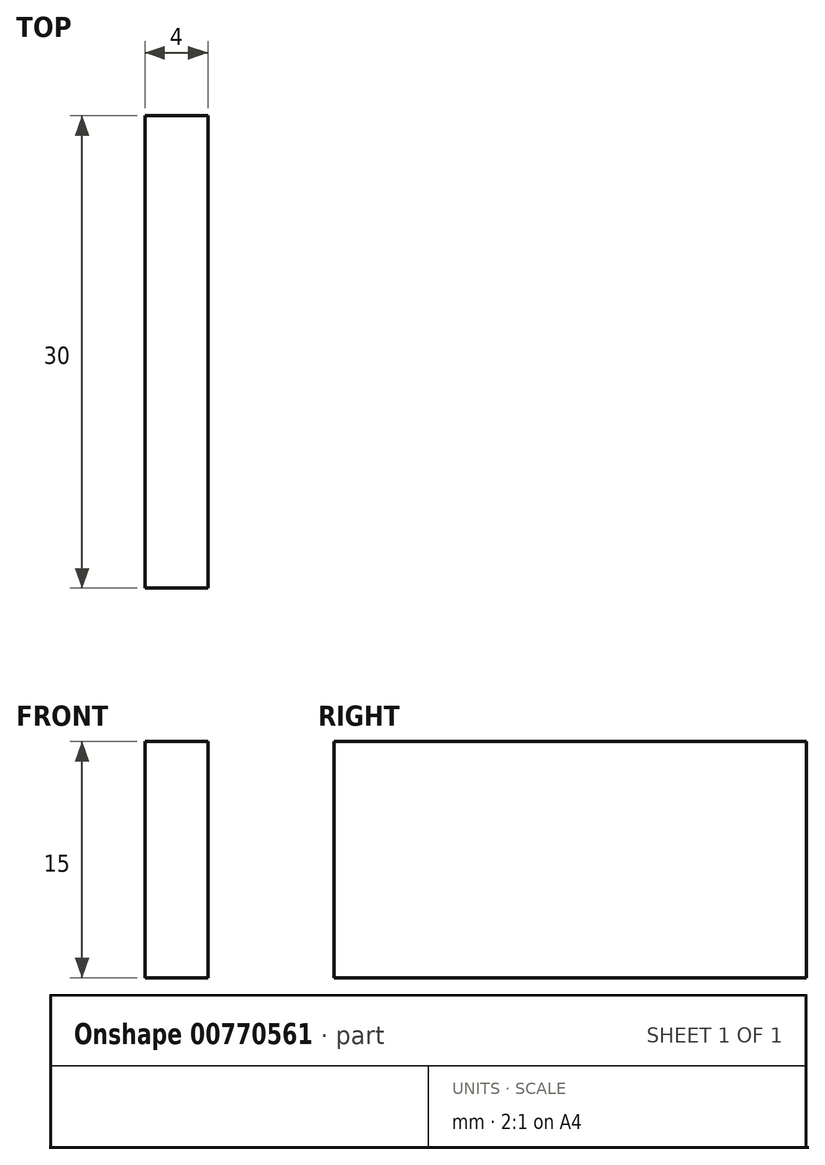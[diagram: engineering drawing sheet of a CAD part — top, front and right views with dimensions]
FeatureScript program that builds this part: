
annotation { "Feature Type Name" : "Feature", "Feature Type Description" : "" }
export const myFeature = defineFeature(function(context is Context, id is Id, definition is map)
    precondition{}
    {
        {
            var Q0;
            Q0=qCreatedBy(makeId("Right.planeOp"),FACE);
            var sketch = newSketch(context, id + "F0", { "sketchPlane" : qUnion([Q0])});
            skLineSegment(sketch, "E0.bottom", {"start": v(0, 0) * mm, "end": v(-30, 0) * mm});
            skLineSegment(sketch, "E0.top", {"start": v(0, 15) * mm, "end": v(-30, 15) * mm});
            skLineSegment(sketch, "E0.left", {"start": v(0, 0) * mm, "end": v(0, 15) * mm});
            skLineSegment(sketch, "E0.right", {"start": v(-30, 0) * mm, "end": v(-30, 15) * mm});
            skSolve(sketch);
        }
        {
            var Q0;
            Q0 = qSketchRegion(id + "F0", true);
            extrude(context, id + "F1", {"entities" : qUnion([Q0]), "depth" : 4 * mm, "offsetDistance" : 25 * mm});
        }
    });
